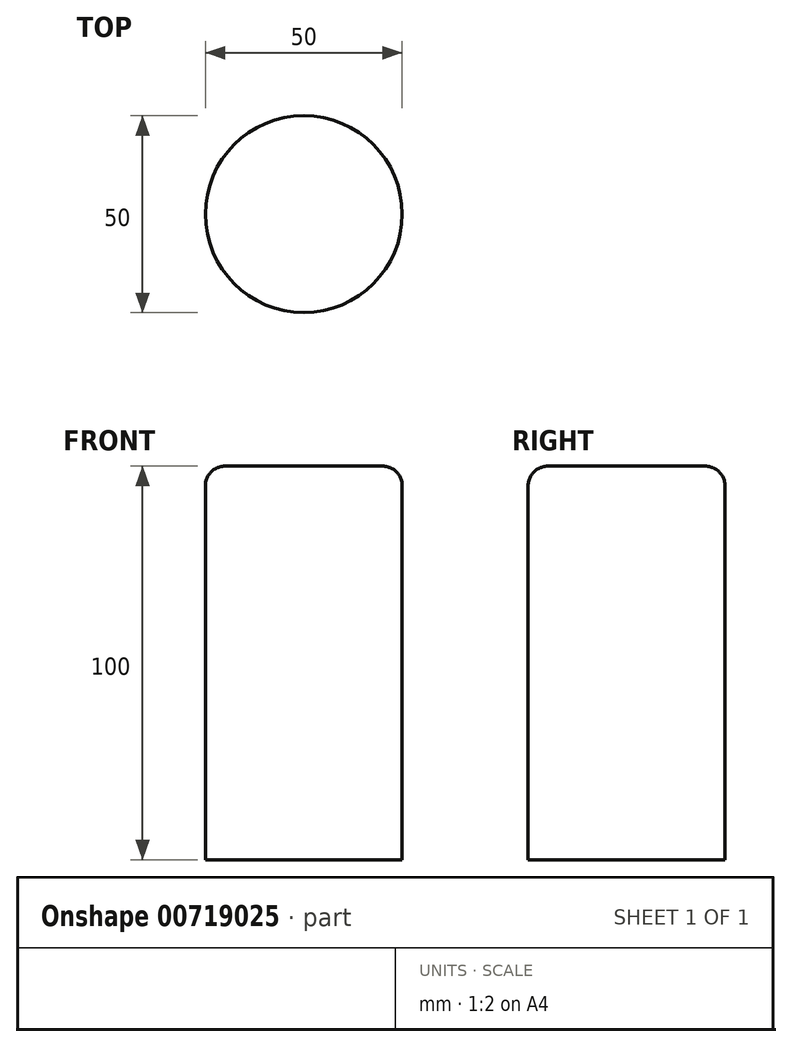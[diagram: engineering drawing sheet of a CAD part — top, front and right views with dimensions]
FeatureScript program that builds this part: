
annotation { "Feature Type Name" : "Feature", "Feature Type Description" : "" }
export const myFeature = defineFeature(function(context is Context, id is Id, definition is map)
    precondition{}
    {
        {
            var Q0;
            Q0=qCreatedBy(makeId("Top.planeOp"),FACE);
            var sketch = newSketch(context, id + "F0", { "sketchPlane" : qUnion([Q0])});
            skCircle(sketch, "E0", {"center": v(0, 0) * mm, "radius": 25 * mm});
            skSolve(sketch);
        }
        {
            var Q0;
            Q0=makeQuery(id+"F0.imprint","IMPRINT",FACE,{"disambiguationData":[TD([[makeQuery(id+"F0.imprint","IMPRINT",EDGE,{"derivedFrom":sQuery(id+"F0.wireOp",EDGE,"E0")}),1.0]])]});
            extrude(context, id + "F1", {"entities" : qUnion([Q0]), "depth" : 60 * mm, "offsetDistance" : 25 * mm, "hasSecondDirection" : true, "secondDirectionOppositeDirection" : true, "secondDirectionDepth" : 40 * mm});
        }
        {
            var Q0;
            Q0=makeQuery(id+"F1.opExtrude","CAP_EDGE",EDGE,{"disambiguationData":[OSD([sQuery(id+"F0.wireOp",EDGE,"E0")])],"isStart":false});
            fillet(context, id + "F2", {"entities" : qUnion([Q0]), "radius" : 5 * mm, "tangentPropagation" : true, "allowEdgeOverflow" : false});
        }
    });
